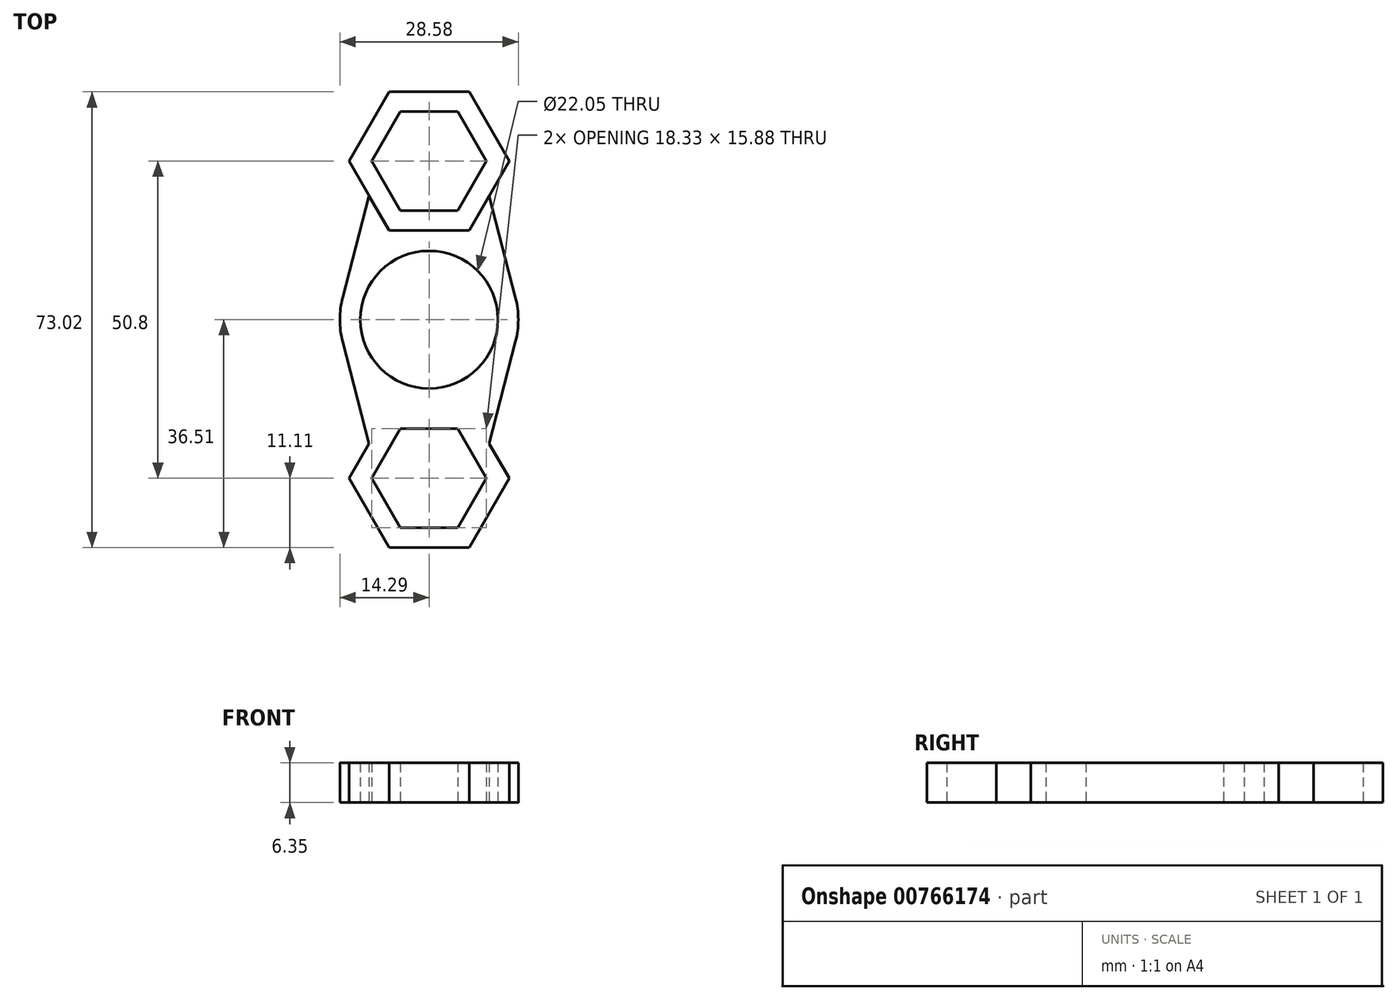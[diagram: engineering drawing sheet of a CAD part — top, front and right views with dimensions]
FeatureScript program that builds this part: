
annotation { "Feature Type Name" : "Feature", "Feature Type Description" : "" }
export const myFeature = defineFeature(function(context is Context, id is Id, definition is map)
    precondition{}
    {
        {
            var Q0;
            Q0=qCreatedBy(makeId("Top.planeOp"),FACE);
            var sketch = newSketch(context, id + "F0", { "sketchPlane" : qUnion([Q0])});
            skCircle(sketch, "E0", {"center": v(0, 0) * mm, "radius": 11.02 * mm});
            skCircle(sketch, "E1", {"center": v(0, 0) * mm, "radius": 14.29 * mm});
            skCircle(sketch, "E2.cCircle", {"center": v(0, 25.4) * mm, "radius": 7.94 * mm, "construction": true});
            skLineSegment(sketch, "E2.0", {"start": v(4.58, 17.46) * mm, "end": v(-4.58, 17.46) * mm});
            skLineSegment(sketch, "E2.1", {"start": v(-4.58, 17.46) * mm, "end": v(-9.17, 25.4) * mm});
            skLineSegment(sketch, "E2.2", {"start": v(-9.17, 25.4) * mm, "end": v(-4.58, 33.34) * mm});
            skLineSegment(sketch, "E2.3", {"start": v(-4.58, 33.34) * mm, "end": v(4.58, 33.34) * mm});
            skLineSegment(sketch, "E2.4", {"start": v(4.58, 33.34) * mm, "end": v(9.17, 25.4) * mm});
            skLineSegment(sketch, "E2.5", {"start": v(9.17, 25.4) * mm, "end": v(4.58, 17.46) * mm});
            skPoint(sketch, "E2.0.midPoint", {"position": v(0, 17.46) * mm});
            skCircle(sketch, "E3.cCircle", {"center": v(0, 25.4) * mm, "radius": 11.11 * mm, "construction": true});
            skLineSegment(sketch, "E3.0", {"start": v(6.42, 14.29) * mm, "end": v(-6.42, 14.29) * mm});
            skLineSegment(sketch, "E3.1", {"start": v(-6.42, 14.29) * mm, "end": v(-12.83, 25.4) * mm});
            skLineSegment(sketch, "E3.2", {"start": v(-12.83, 25.4) * mm, "end": v(-6.42, 36.51) * mm});
            skLineSegment(sketch, "E3.3", {"start": v(-6.42, 36.51) * mm, "end": v(6.42, 36.51) * mm});
            skLineSegment(sketch, "E3.4", {"start": v(6.42, 36.51) * mm, "end": v(12.83, 25.4) * mm});
            skLineSegment(sketch, "E3.5", {"start": v(12.83, 25.4) * mm, "end": v(6.42, 14.29) * mm});
            skPoint(sketch, "E3.0.midPoint", {"position": v(0, 14.29) * mm});
            skCircle(sketch, "E4.1.0", {"center": v(0, -25.4) * mm, "radius": 11.11 * mm, "construction": true});
            skLineSegment(sketch, "E4.1.1", {"start": v(6.42, -14.29) * mm, "end": v(12.83, -25.4) * mm});
            skPoint(sketch, "E4.1.2", {"position": v(0, -17.46) * mm});
            skCircle(sketch, "E4.1.3", {"center": v(0, -25.4) * mm, "radius": 7.94 * mm, "construction": true});
            skLineSegment(sketch, "E4.1.4", {"start": v(-12.83, -25.4) * mm, "end": v(-6.42, -14.29) * mm});
            skLineSegment(sketch, "E4.1.5", {"start": v(9.17, -25.4) * mm, "end": v(4.58, -33.34) * mm});
            skLineSegment(sketch, "E4.1.6", {"start": v(4.58, -33.34) * mm, "end": v(-4.58, -33.34) * mm});
            skLineSegment(sketch, "E4.1.7", {"start": v(-4.58, -33.34) * mm, "end": v(-9.17, -25.4) * mm});
            skLineSegment(sketch, "E4.1.8", {"start": v(-9.17, -25.4) * mm, "end": v(-4.58, -17.46) * mm});
            skLineSegment(sketch, "E4.1.9", {"start": v(12.83, -25.4) * mm, "end": v(6.42, -36.51) * mm});
            skLineSegment(sketch, "E4.1.10", {"start": v(4.58, -17.46) * mm, "end": v(9.17, -25.4) * mm});
            skPoint(sketch, "E4.1.11", {"position": v(0, -14.29) * mm});
            skLineSegment(sketch, "E4.1.12", {"start": v(-6.42, -36.51) * mm, "end": v(-12.83, -25.4) * mm});
            skLineSegment(sketch, "E4.1.13", {"start": v(6.42, -36.51) * mm, "end": v(-6.42, -36.51) * mm});
            skLineSegment(sketch, "E4.1.14", {"start": v(-4.58, -17.46) * mm, "end": v(4.58, -17.46) * mm});
            skLineSegment(sketch, "E4.1.15", {"start": v(-6.42, -14.29) * mm, "end": v(6.42, -14.29) * mm});
            skSolve(sketch);
        }
        {
            var Q0;
            Q0=qCreatedBy(makeId("Top.planeOp"),FACE);
            var sketch = newSketch(context, id + "F1", { "sketchPlane" : qUnion([Q0])});
            skLineSegment(sketch, "E5.0", {"start": v(6.42, 14.29) * mm, "end": v(-6.42, 14.29) * mm});
            skLineSegment(sketch, "E5.1", {"start": v(12.83, -25.4) * mm, "end": v(6.42, -36.51) * mm});
            skLineSegment(sketch, "E5.2", {"start": v(-6.42, -36.51) * mm, "end": v(-12.83, -25.4) * mm});
            skLineSegment(sketch, "E5.3", {"start": v(-12.83, -25.4) * mm, "end": v(-6.42, -14.29) * mm});
            skLineSegment(sketch, "E5.4", {"start": v(4.58, -17.46) * mm, "end": v(9.17, -25.4) * mm});
            skLineSegment(sketch, "E5.5", {"start": v(-4.58, 17.46) * mm, "end": v(-9.17, 25.4) * mm});
            skLineSegment(sketch, "E5.6", {"start": v(4.58, 17.46) * mm, "end": v(-4.58, 17.46) * mm});
            skLineSegment(sketch, "E5.7", {"start": v(4.58, -33.34) * mm, "end": v(-4.58, -33.34) * mm});
            skCircle(sketch, "E5.8", {"center": v(0, 25.4) * mm, "radius": 7.94 * mm});
            skLineSegment(sketch, "E5.9", {"start": v(-6.42, 36.51) * mm, "end": v(6.42, 36.51) * mm});
            skCircle(sketch, "E5.10", {"center": v(0, 0) * mm, "radius": 11.02 * mm});
            skLineSegment(sketch, "E5.11", {"start": v(12.83, 25.4) * mm, "end": v(6.42, 14.29) * mm});
            skLineSegment(sketch, "E5.12", {"start": v(6.42, 36.51) * mm, "end": v(12.83, 25.4) * mm});
            skLineSegment(sketch, "E5.13", {"start": v(6.42, -36.51) * mm, "end": v(-6.42, -36.51) * mm});
            skLineSegment(sketch, "E5.14", {"start": v(-6.42, -14.29) * mm, "end": v(6.42, -14.29) * mm});
            skCircle(sketch, "E5.15", {"center": v(0, -25.4) * mm, "radius": 11.11 * mm});
            skCircle(sketch, "E5.16", {"center": v(0, 25.4) * mm, "radius": 11.11 * mm});
            skLineSegment(sketch, "E5.17", {"start": v(9.17, 25.4) * mm, "end": v(4.58, 17.46) * mm});
            skLineSegment(sketch, "E5.18", {"start": v(4.58, 33.34) * mm, "end": v(9.17, 25.4) * mm});
            skLineSegment(sketch, "E5.19", {"start": v(-4.58, 33.34) * mm, "end": v(4.58, 33.34) * mm});
            skLineSegment(sketch, "E5.20", {"start": v(-9.17, 25.4) * mm, "end": v(-4.58, 33.34) * mm});
            skLineSegment(sketch, "E5.21", {"start": v(9.17, -25.4) * mm, "end": v(4.58, -33.34) * mm});
            skLineSegment(sketch, "E5.22", {"start": v(-9.17, -25.4) * mm, "end": v(-4.58, -17.46) * mm});
            skLineSegment(sketch, "E5.23", {"start": v(-4.58, -33.34) * mm, "end": v(-9.17, -25.4) * mm});
            skLineSegment(sketch, "E5.24", {"start": v(-12.83, 25.4) * mm, "end": v(-6.42, 36.51) * mm});
            skLineSegment(sketch, "E5.25", {"start": v(6.42, -14.29) * mm, "end": v(12.83, -25.4) * mm});
            skCircle(sketch, "E5.26", {"center": v(0, 0) * mm, "radius": 14.29 * mm});
            skLineSegment(sketch, "E5.27", {"start": v(-6.42, 14.29) * mm, "end": v(-12.83, 25.4) * mm});
            skLineSegment(sketch, "E5.28", {"start": v(-4.58, -17.46) * mm, "end": v(4.58, -17.46) * mm});
            skCircle(sketch, "E5.29", {"center": v(0, -25.4) * mm, "radius": 7.94 * mm});
            skLineSegment(sketch, "E6", {"start": v(-9.62, 19.84) * mm, "end": v(-14.76, 0) * mm});
            skLineSegment(sketch, "E7", {"start": v(-14.76, 0) * mm, "end": v(-9.62, -19.84) * mm});
            skLineSegment(sketch, "E8", {"start": v(9.62, 19.84) * mm, "end": v(14.76, 0) * mm});
            skLineSegment(sketch, "E9", {"start": v(14.76, 0) * mm, "end": v(9.62, -19.84) * mm});
            skSolve(sketch);
        }
        {
            var Q0;
            Q0=makeQuery(id+"F0.imprint","IMPRINT",FACE,{"disambiguationData":[TD([[makeQuery(id+"F0.imprint","IMPRINT",EDGE,{"derivedFrom":sQuery(id+"F0.wireOp",EDGE,"E2.0")}),1.0]])]});
            var Q1;
            {var subQ0=sQuery(id+"F1.wireOp",EDGE,"E5.27");var subQ1=sQuery(id+"F1.wireOp",EDGE,"E5.0");var subQ2=makeQuery(id+"F1.imprint","INTERSECT",VERTEX,{"derivedFrom":[subQ1,subQ0]});Q1=makeQuery(id+"F1.imprint","IMPRINT",FACE,{"disambiguationData":[TD([[makeQuery(id+"F1.imprint","IMPRINT",EDGE,{"disambiguationData":[TD([[subQ2,1.0]])],"derivedFrom":subQ1}),1.0]])]});}
            var Q2;
            {var subQ0=sQuery(id+"F1.wireOp",EDGE,"E5.11");var subQ1=sQuery(id+"F1.wireOp",EDGE,"E5.0");var subQ2=makeQuery(id+"F1.imprint","INTERSECT",VERTEX,{"derivedFrom":[subQ1,subQ0]});Q2=makeQuery(id+"F1.imprint","IMPRINT",FACE,{"disambiguationData":[TD([[makeQuery(id+"F1.imprint","IMPRINT",EDGE,{"disambiguationData":[TD([[subQ2,-1.0]])],"derivedFrom":subQ1}),1.0]])]});}
            var Q3;
            Q3=makeQuery(id+"F1.imprint","IMPRINT",FACE,{"disambiguationData":[TD([[makeQuery(id+"F1.imprint","IMPRINT",EDGE,{"derivedFrom":sQuery(id+"F1.wireOp",EDGE,"E5.10")}),-1.0]])]});
            var Q4;
            {var subQ0=sQuery(id+"F1.wireOp",EDGE,"E5.25");var subQ1=sQuery(id+"F1.wireOp",EDGE,"E5.14");var subQ2=makeQuery(id+"F1.imprint","INTERSECT",VERTEX,{"derivedFrom":[subQ1,subQ0]});Q4=makeQuery(id+"F1.imprint","IMPRINT",FACE,{"disambiguationData":[TD([[makeQuery(id+"F1.imprint","IMPRINT",EDGE,{"disambiguationData":[TD([[subQ2,1.0]])],"derivedFrom":subQ1}),1.0]])]});}
            var Q5;
            {var subQ0=sQuery(id+"F1.wireOp",EDGE,"E5.14");var subQ1=sQuery(id+"F1.wireOp",EDGE,"E5.3");var subQ2=makeQuery(id+"F1.imprint","INTERSECT",VERTEX,{"derivedFrom":[subQ1,subQ0]});Q5=makeQuery(id+"F1.imprint","IMPRINT",FACE,{"disambiguationData":[TD([[makeQuery(id+"F1.imprint","IMPRINT",EDGE,{"disambiguationData":[TD([[subQ2,1.0]])],"derivedFrom":subQ1}),1.0]])]});}
            var Q6;
            {var subQ14=sQuery(id+"F1.wireOp",EDGE,"E5.28");var subQ17=sQuery(id+"F1.wireOp",EDGE,"E5.4");var subQ18=makeQuery(id+"F1.imprint","INTERSECT",VERTEX,{"derivedFrom":[subQ17,subQ14]});Q6=makeQuery(id+"F1.imprint","IMPRINT",FACE,{"disambiguationData":[TD([[makeQuery(id+"F1.imprint","IMPRINT",EDGE,{"disambiguationData":[TD([[subQ18,-1.0]])],"derivedFrom":subQ17}),1.0]])]});}
            var Q7;
            {var subQ0=sQuery(id+"F1.wireOp",EDGE,"E5.3");var subQ1=sQuery(id+"F1.wireOp",EDGE,"E5.2");var subQ2=makeQuery(id+"F1.imprint","INTERSECT",VERTEX,{"derivedFrom":[subQ1,subQ0]});Q7=makeQuery(id+"F1.imprint","IMPRINT",FACE,{"disambiguationData":[TD([[makeQuery(id+"F1.imprint","IMPRINT",EDGE,{"disambiguationData":[TD([[subQ2,1.0]])],"derivedFrom":subQ1}),-1.0]])]});}
            var Q8;
            {var subQ0=sQuery(id+"F1.wireOp",EDGE,"E5.13");var subQ1=sQuery(id+"F1.wireOp",EDGE,"E5.2");var subQ2=makeQuery(id+"F1.imprint","INTERSECT",VERTEX,{"derivedFrom":[subQ1,subQ0]});Q8=makeQuery(id+"F1.imprint","IMPRINT",FACE,{"disambiguationData":[TD([[makeQuery(id+"F1.imprint","IMPRINT",EDGE,{"disambiguationData":[TD([[subQ2,-1.0]])],"derivedFrom":subQ1}),-1.0]])]});}
            var Q9;
            {var subQ0=sQuery(id+"F1.wireOp",EDGE,"E5.13");var subQ1=sQuery(id+"F1.wireOp",EDGE,"E5.1");var subQ2=makeQuery(id+"F1.imprint","INTERSECT",VERTEX,{"derivedFrom":[subQ1,subQ0]});Q9=makeQuery(id+"F1.imprint","IMPRINT",FACE,{"disambiguationData":[TD([[makeQuery(id+"F1.imprint","IMPRINT",EDGE,{"disambiguationData":[TD([[subQ2,1.0]])],"derivedFrom":subQ1}),-1.0]])]});}
            var Q10;
            {var subQ0=sQuery(id+"F1.wireOp",EDGE,"E5.25");var subQ1=sQuery(id+"F1.wireOp",EDGE,"E5.1");var subQ2=makeQuery(id+"F1.imprint","INTERSECT",VERTEX,{"derivedFrom":[subQ1,subQ0]});Q10=makeQuery(id+"F1.imprint","IMPRINT",FACE,{"disambiguationData":[TD([[makeQuery(id+"F1.imprint","IMPRINT",EDGE,{"disambiguationData":[TD([[subQ2,-1.0]])],"derivedFrom":subQ1}),-1.0]])]});}
            var Q11;
            {var subQ0=sQuery(id+"F1.wireOp",EDGE,"E5.25");var subQ1=sQuery(id+"F1.wireOp",EDGE,"E5.14");var subQ2=makeQuery(id+"F1.imprint","INTERSECT",VERTEX,{"derivedFrom":[subQ1,subQ0]});Q11=makeQuery(id+"F1.imprint","IMPRINT",FACE,{"disambiguationData":[TD([[makeQuery(id+"F1.imprint","IMPRINT",EDGE,{"disambiguationData":[TD([[subQ2,1.0]])],"derivedFrom":subQ1}),-1.0]])]});}
            var Q12;
            {var subQ0=sQuery(id+"F1.wireOp",EDGE,"E5.14");var subQ1=sQuery(id+"F1.wireOp",EDGE,"E5.3");var subQ2=makeQuery(id+"F1.imprint","INTERSECT",VERTEX,{"derivedFrom":[subQ1,subQ0]});Q12=makeQuery(id+"F1.imprint","IMPRINT",FACE,{"disambiguationData":[TD([[makeQuery(id+"F1.imprint","IMPRINT",EDGE,{"disambiguationData":[TD([[subQ2,1.0]])],"derivedFrom":subQ1}),-1.0]])]});}
            extrude(context, id + "F2", {"entities" : qUnion([Q0, Q1, Q2, Q3, Q4, Q5, Q6, Q7, Q8, Q9, Q10, Q11, Q12]), "depth" : 6.35 * mm, "offsetDistance" : 25.4 * mm});
        }
    });
